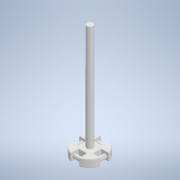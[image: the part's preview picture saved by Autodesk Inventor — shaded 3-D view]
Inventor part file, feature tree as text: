
AUTODESK INVENTOR PART (.ipt)
format: ipt  version: 2022 (Build 260153000, 153)  size: 236,032 bytes
history: native  units: mm
features: extrude x4, sketch x4, pattern_circular x1, fillet x1
ambient origin geometry x8: Origin, YZ Plane, XZ Plane, XY Plane, X Axis, Y Axis, Z Axis, Center Point
bodies: Solid1 (feature_tree)
feature tree (10):
  extrude  "Extrusion1"  Depth=3.33mm
  extrude  "Extrusion2"  Depth=3.332mm TaperAngle=0.0deg
  pattern_circular  "Circular Pattern1"  Count=4 Angle=360.0deg
  extrude  "Extrusion3"  Depth=0.3mm
  fillet  "Fillet1"  Radius=30.0mm
  extrude  "Extrusion4"  Depth=0.3mm
  sketch  "Sketch1"  dims[d0=13.33mm d1=3.33mm]
  sketch  "Sketch2"  dims[d2=40.0mm d4=360.0deg d6=3.332mm d7=0.0mm]
  sketch  "Sketch3"  dims[d8=1.66mm]
  sketch  "Sketch4"  dims[d9=3.332mm d10=0.0mm d11=40.0mm d12=360.0deg d14=2.66mm d15=30.0mm d16=0.0mm d17=0.3mm d18=15.0mm d19=0.0mm]
